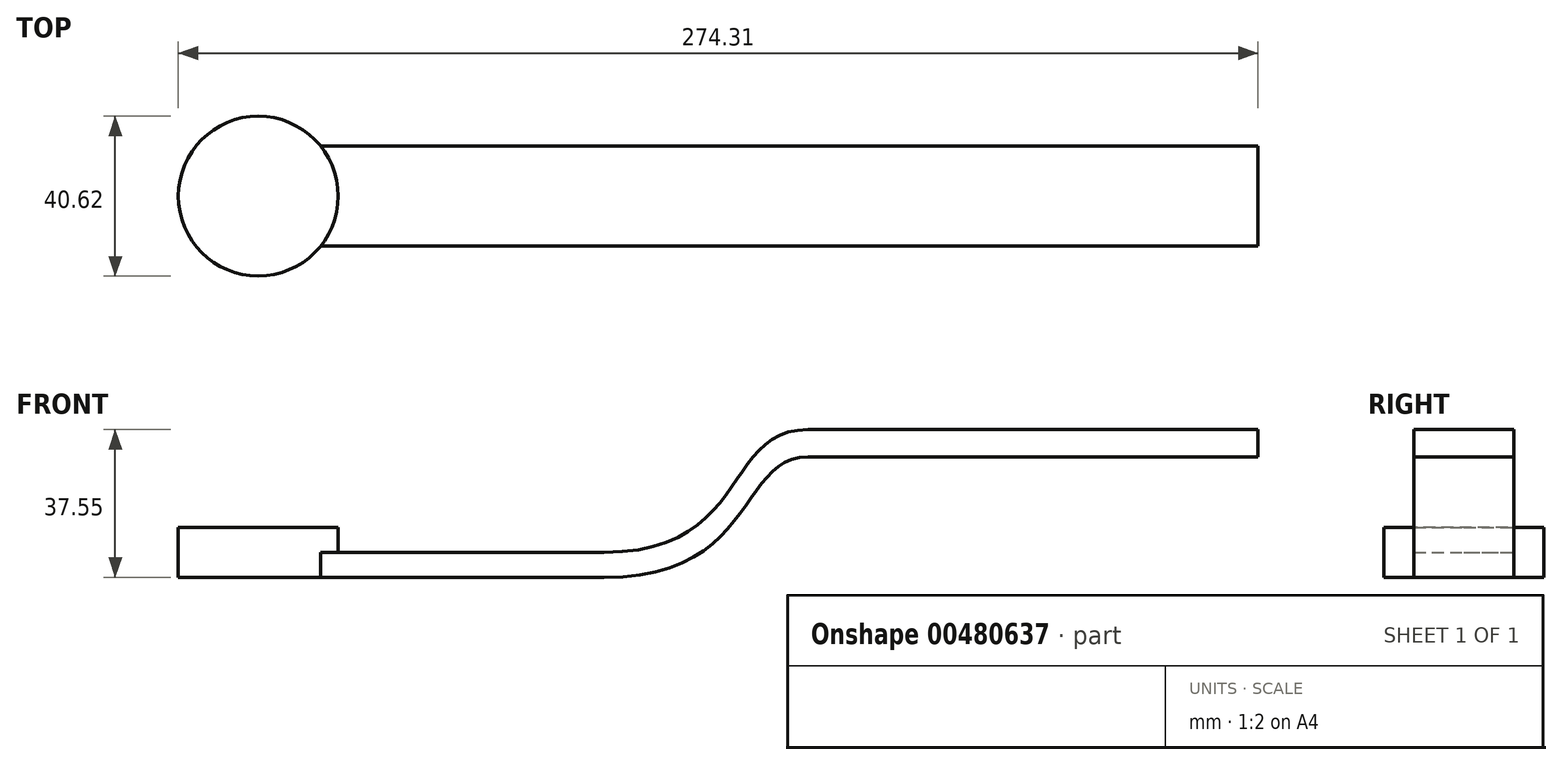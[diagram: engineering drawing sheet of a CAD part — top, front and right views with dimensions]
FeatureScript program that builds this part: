
annotation { "Feature Type Name" : "Feature", "Feature Type Description" : "" }
export const myFeature = defineFeature(function(context is Context, id is Id, definition is map)
    precondition{}
    {
        {
            var Q0;
            Q0=qCreatedBy(makeId("Front.planeOp"),FACE);
            var sketch = newSketch(context, id + "F0", { "sketchPlane" : qUnion([Q0])});
            skLineSegment(sketch, "E0.bottom", {"start": v(-10.15, 6.35) * mm, "end": v(10.15, 6.35) * mm});
            skLineSegment(sketch, "E0.top", {"start": v(-10.15, -6.35) * mm, "end": v(10.15, -6.35) * mm});
            skLineSegment(sketch, "E0.left", {"start": v(-10.15, 6.35) * mm, "end": v(-10.15, -6.35) * mm});
            skLineSegment(sketch, "E0.right", {"start": v(10.15, 6.35) * mm, "end": v(10.15, -6.35) * mm});
            skPoint(sketch, "E0.middle", {"position": v(0, 0) * mm});
            skLineSegment(sketch, "E1.bottom", {"start": v(10.15, -6.35) * mm, "end": v(98, -6.35) * mm});
            skLineSegment(sketch, "E1.top", {"start": v(10.15, 0) * mm, "end": v(98, 0) * mm});
            skLineSegment(sketch, "E1.left", {"start": v(10.15, -6.35) * mm, "end": v(10.15, 0) * mm});
            skLineSegment(sketch, "E1.right", {"start": v(98, -6.35) * mm, "end": v(98, 0) * mm});
            skLineSegment(sketch, "E2.bottom", {"start": v(264.16, 24.22) * mm, "end": v(149.86, 24.22) * mm});
            skLineSegment(sketch, "E2.top", {"start": v(264.16, 31.2) * mm, "end": v(149.86, 31.2) * mm});
            skLineSegment(sketch, "E2.left", {"start": v(264.16, 24.22) * mm, "end": v(264.16, 31.2) * mm});
            skLineSegment(sketch, "E2.right", {"start": v(149.86, 24.22) * mm, "end": v(149.86, 31.2) * mm});
            skFitSpline(sketch, "E3", {"points": [v(98, -6.35) * mm, v(149.86, 24.22) * mm], "startDerivative": vector(116.78, 0) * mm, "endDerivative": vector(53.5, 0) * mm});
            skFitSpline(sketch, "E4", {"points": [v(98, 0) * mm, v(149.86, 31.2) * mm], "startDerivative": vector(111.89, 0) * mm, "endDerivative": vector(65.65, 0) * mm});
            skSolve(sketch);
        }
        {
            var Q0;
            Q0=makeQuery(id+"F0.imprint","IMPRINT",FACE,{"disambiguationData":[TD([[makeQuery(id+"F0.imprint","IMPRINT",EDGE,{"derivedFrom":sQuery(id+"F0.wireOp",EDGE,"E1.bottom")}),1.0]])]});
            var Q1;
            Q1=makeQuery(id+"F0.imprint","IMPRINT",FACE,{"disambiguationData":[TD([[makeQuery(id+"F0.imprint","IMPRINT",EDGE,{"derivedFrom":sQuery(id+"F0.wireOp",EDGE,"E1.right")}),-1.0]])]});
            var Q2;
            Q2=makeQuery(id+"F0.imprint","IMPRINT",FACE,{"disambiguationData":[TD([[makeQuery(id+"F0.imprint","IMPRINT",EDGE,{"derivedFrom":sQuery(id+"F0.wireOp",EDGE,"E2.bottom")}),-1.0]])]});
            extrude(context, id + "F1", {"entities" : qUnion([Q0, Q1, Q2]), "depth" : 25.4 * mm, "symmetric" : true});
        }
        {
            var Q0;
            Q0=makeQuery(id+"F0.imprint","IMPRINT",FACE,{"disambiguationData":[TD([[makeQuery(id+"F0.imprint","IMPRINT",EDGE,{"derivedFrom":sQuery(id+"F0.wireOp",EDGE,"E0.bottom")}),-1.0]])]});
            var Q1;
            Q1=sQuery(id+"F0.wireOp",EDGE,"E0.right");
            revolve(context, id + "F2", {"operationType" : NewBodyOperationType.ADD, "entities" : qUnion([Q0]), "axis" : qUnion([Q1]), "revolveType" : RevolveType.FULL});
        }
    });
